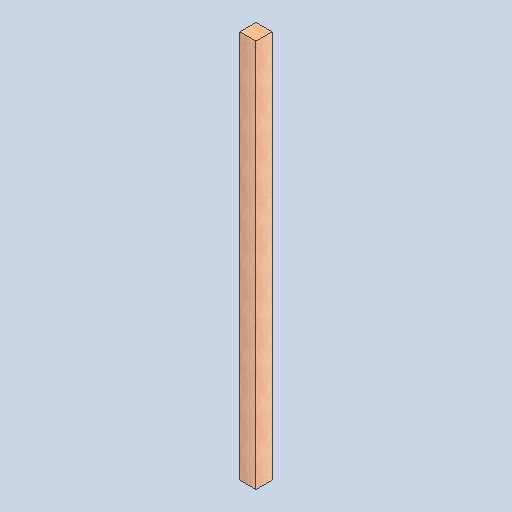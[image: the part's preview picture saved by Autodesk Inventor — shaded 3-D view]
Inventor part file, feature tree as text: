
AUTODESK INVENTOR PART (.ipt)
format: ipt  version: 2025 (Build 290162000, 162)  size: 295,936 bytes
history: native  units: in
note: dims shown in document units (in); Inventor stores cm internally (conversion verified against a paired STEP export)
features: extrude x1, sketch x1
ambient origin geometry x8: Origin, YZ Plane, XZ Plane, XY Plane, X Axis, Y Axis, Z Axis, Center Point
bodies: Solid1 (feature_tree)
feature tree (2):
  extrude  "Extrusion1"  Depth=4.0in
  sketch  "Sketch1"  dims[d0=4.0in d1=4.0in d2=96.0in d3=0.0in d4=0.5in d5=0.0344in d6=0.5in d7=0.0344in]
